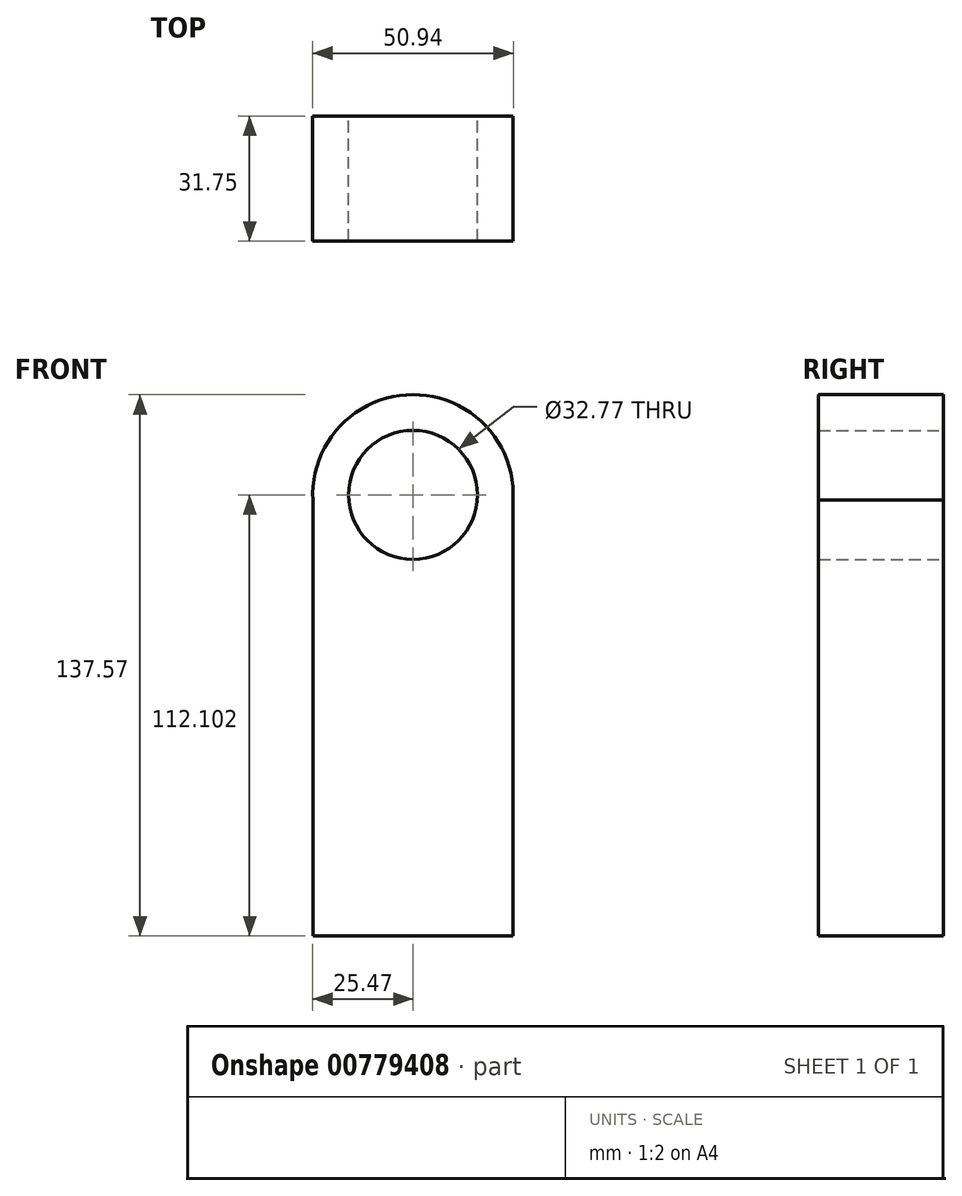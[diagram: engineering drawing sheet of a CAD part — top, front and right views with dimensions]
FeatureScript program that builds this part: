
annotation { "Feature Type Name" : "Feature", "Feature Type Description" : "" }
export const myFeature = defineFeature(function(context is Context, id is Id, definition is map)
    precondition{}
    {
        {
            var Q0;
            Q0=qCreatedBy(makeId("Front.planeOp"),FACE);
            var sketch = newSketch(context, id + "F0", { "sketchPlane" : qUnion([Q0])});
            skLineSegment(sketch, "E0.top", {"start": v(-25.43, -56.05) * mm, "end": v(25.43, -56.05) * mm});
            skLineSegment(sketch, "E0.left", {"start": v(-25.43, 56.05) * mm, "end": v(-25.43, -56.05) * mm});
            skLineSegment(sketch, "E0.right", {"start": v(25.43, 56.05) * mm, "end": v(25.43, -56.05) * mm});
            skPoint(sketch, "E0.middle", {"position": v(0, 0) * mm});
            skArc(sketch, "E1", {"start": v(25.43, 54.74) * mm, "mid": v(0, 81.52) * mm, "end": v(-25.43, 54.74) * mm});
            skCircle(sketch, "E2", {"center": v(0, 56.05) * mm, "radius": 16.38 * mm});
            skSolve(sketch);
        }
        {
            var Q0;
            {var subQ2=sQuery(id+"F0.wireOp",EDGE,"E0.top");Q0=makeQuery(id+"F0.imprint","IMPRINT",FACE,{"disambiguationData":[TD([[makeQuery(id+"F0.imprint","IMPRINT",EDGE,{"derivedFrom":subQ2}),1.0]])]});}
            extrude(context, id + "F1", {"entities" : qUnion([Q0]), "depth" : 31.75 * mm, "offsetDistance" : 25.4 * mm});
        }
    });
